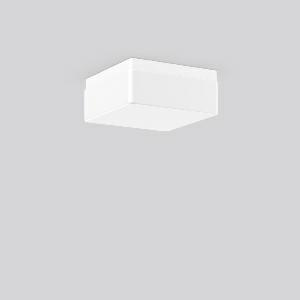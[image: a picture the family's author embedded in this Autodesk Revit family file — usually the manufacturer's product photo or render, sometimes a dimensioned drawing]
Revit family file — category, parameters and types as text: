
# Revit family: quadrat_211412_002_1_1be4
name_source: partatom
category: Lighting Fixtures
units: mm (PartAtom-declared; Revit-internal decimal feet)

## family parameters
Cut with Voids When Loaded = No
Host = Face
Light Source = No
Part Type = Normal
Room Calculation Point = No
Round Connector Dimension = Use Diameter
Shared = No

## types (1)
- QUADRAT (1 x LED Modul 840, 1100 lm, 4000)
    Apparent Load = 11 VA
    CIE Flux Codes = 38 67 88 80 100
    Color Rendering = 80
    Color Temperature = 4000
    Default Elevation = 1800 mm
    Description = Series: QUADRAT
Square surface-mounted luminaire in classic design. Base: plastic. Opal glass: mouth-blown, satin finish. Diffuser fastening: spring system. Suitable for Ceiling mounting, Wall (surface). IP 43 ceiling mounting, IP 44 wall mounting. 
Colour: white
Length: 280 mm
Width: 280 mm
Height: 120 mm
Lamp: LED exchangeable
Socket: without socket
Colour temperature: 4000K
Colour rendering index (CRI): 80
System power: 11 W
Rated luminous flux: 1100 lm
Luminous efficiency: 100 lm/W
Control gear: AC Strom, dim.Ph.an-/abschnitt
Protection class: I
Type of protection: IP 43
    Height = 120 mm
    Lamp = 1 x LED Modul 840
    Lamp Light Flux = 1100 lm
    Lamp count = 1
    Length = 280 mm
    Lifetime = 50000 h
    Luminous efficacy = 100 lm/W
    Manufacturer = RZB
    ModVariant = No
    Model = 211412.002.1
    Mounting Place = Ceiling, Wall
    Mounting Type = Surface mounted
    Number of Poles = 1
    OnlyDefault = Yes
    Power Factor = 1
    Product Name = QUADRAT
    Product group = Surface mounted ceiling and wall luminaires
    ProductGroupID = 305
    Protection Class = Protection class I
    Protection Degree = IP 43
    RLX_Detail_Level = 1
    RLX_Emergency_Light_Flux = 0 lm
    RLX_Emergency_Type = 0
    RLX_Emergency_Type_DB = No
    RlxData = <blob elided: 11461 chars, md5=05779deb>
    Socket = socket
    Standby Power = 0 W
    System Light Flux = 1100 lm
    System Power = 11 W
    Type Comments = Product without accessories
    Type Image = 21129.002.jpg
    URL = http://relux.com
    VarID = ---
    Voltage = 230 V
    Voltage Range = 220-240 V
    Weight = 0.00 kg
    Width = 280 mm

## geometry (parser evidence)
native form markers: Sweep x13
no freeform markers — native parametric forms only
